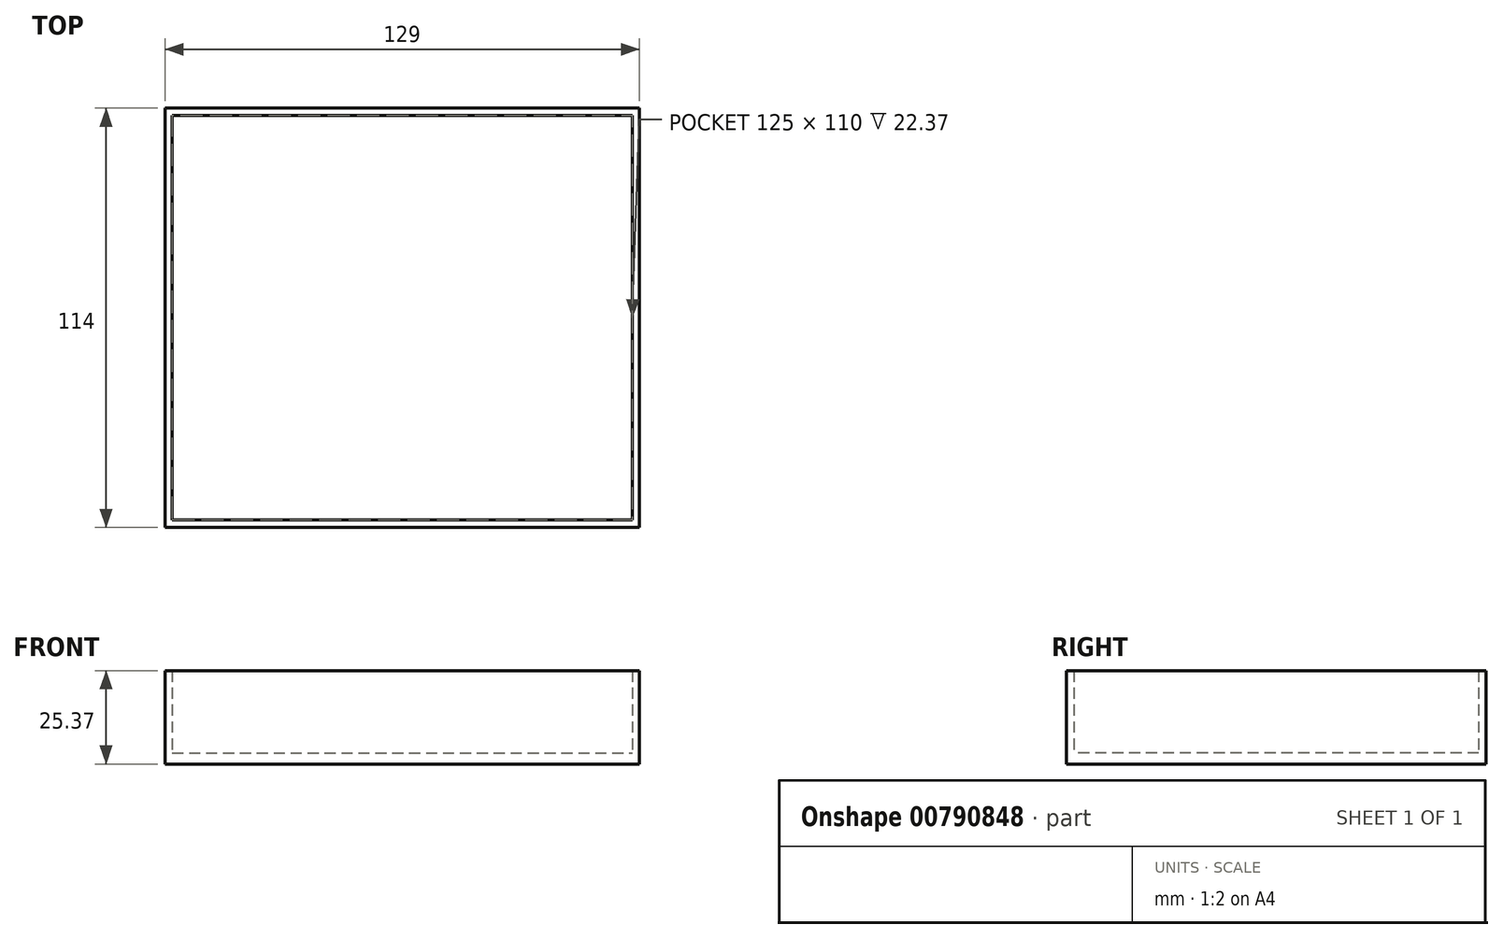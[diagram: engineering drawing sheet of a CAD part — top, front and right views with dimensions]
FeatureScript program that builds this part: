
annotation { "Feature Type Name" : "Feature", "Feature Type Description" : "" }
export const myFeature = defineFeature(function(context is Context, id is Id, definition is map)
    precondition{}
    {
        {
            var Q0;
            Q0=qCreatedBy(makeId("Top.planeOp"),FACE);
            var sketch = newSketch(context, id + "F0", { "sketchPlane" : qUnion([Q0])});
            skLineSegment(sketch, "E0.bottom", {"start": v(-6.23, 107.18) * mm, "end": v(118.77, 107.18) * mm});
            skLineSegment(sketch, "E0.top", {"start": v(-6.23, -2.82) * mm, "end": v(118.77, -2.82) * mm});
            skLineSegment(sketch, "E0.left", {"start": v(-6.23, 107.18) * mm, "end": v(-6.23, -2.82) * mm});
            skLineSegment(sketch, "E0.right", {"start": v(118.77, 107.18) * mm, "end": v(118.77, -2.82) * mm});
            skLineSegment(sketch, "E1.bottom", {"start": v(120.77, 109.18) * mm, "end": v(-8.23, 109.18) * mm});
            skLineSegment(sketch, "E1.top", {"start": v(120.77, -4.82) * mm, "end": v(-8.23, -4.82) * mm});
            skLineSegment(sketch, "E1.left", {"start": v(120.77, 109.18) * mm, "end": v(120.77, -4.82) * mm});
            skLineSegment(sketch, "E1.right", {"start": v(-8.23, 109.18) * mm, "end": v(-8.23, -4.82) * mm});
            skSolve(sketch);
        }
        {
            var Q0;
            Q0 = qSketchRegion(id + "F0", true);
            extrude(context, id + "F1", {"entities" : qUnion([Q0]), "depth" : (19.37 + 3) * mm, "offsetDistance" : 25 * mm});
        }
        {
            var Q0;
            Q0=makeQuery(id+"F1.opExtrude","CAP_FACE",FACE,{"disambiguationData":[OSD([sQuery(id+"F0.wireOp",EDGE,"E0.bottom"),sQuery(id+"F0.wireOp",EDGE,"E0.top"),sQuery(id+"F0.wireOp",EDGE,"E0.left"),sQuery(id+"F0.wireOp",EDGE,"E0.right"),sQuery(id+"F0.wireOp",EDGE,"E1.bottom"),sQuery(id+"F0.wireOp",EDGE,"E1.top"),sQuery(id+"F0.wireOp",EDGE,"E1.left"),sQuery(id+"F0.wireOp",EDGE,"E1.right")])],"isStart":true});
            var sketch = newSketch(context, id + "F2", { "sketchPlane" : qUnion([Q0])});
            skLineSegment(sketch, "E2.bottom", {"start": v(120.77, -109.18) * mm, "end": v(-8.23, -109.18) * mm});
            skLineSegment(sketch, "E2.top", {"start": v(120.77, 4.82) * mm, "end": v(-8.23, 4.82) * mm});
            skLineSegment(sketch, "E2.left", {"start": v(120.77, -109.18) * mm, "end": v(120.77, 4.82) * mm});
            skLineSegment(sketch, "E2.right", {"start": v(-8.23, -109.18) * mm, "end": v(-8.23, 4.82) * mm});
            skSolve(sketch);
        }
        {
            var Q0;
            Q0 = qSketchRegion(id + "F2", true);
            extrude(context, id + "F3", {"entities" : qUnion([Q0]), "operationType" : NewBodyOperationType.ADD, "depth" : 3 * mm, "offsetDistance" : 25 * mm});
        }
    });
